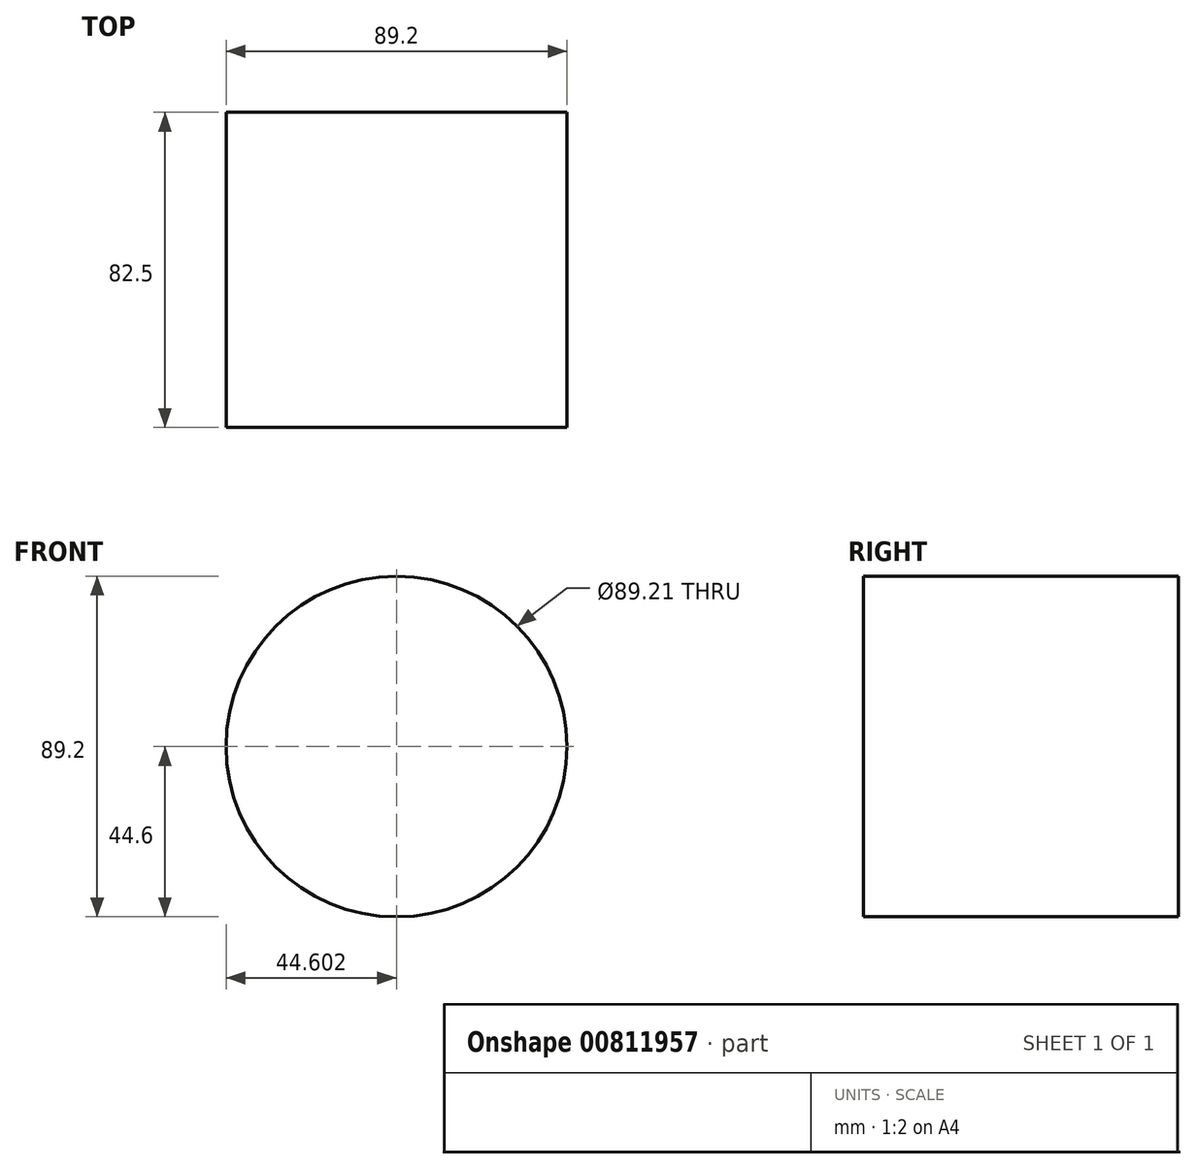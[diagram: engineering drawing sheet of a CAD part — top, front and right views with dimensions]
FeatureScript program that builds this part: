
annotation { "Feature Type Name" : "Feature", "Feature Type Description" : "" }
export const myFeature = defineFeature(function(context is Context, id is Id, definition is map)
    precondition{}
    {
        {
            var Q0;
            Q0=qCreatedBy(makeId("Top.planeOp"),FACE);
            var sketch = newSketch(context, id + "F0", { "sketchPlane" : qUnion([Q0])});
            skLineSegment(sketch, "E0.bottom", {"start": v(22.3, -41.25) * mm, "end": v(-22.3, -41.25) * mm});
            skLineSegment(sketch, "E0.top", {"start": v(22.3, 41.25) * mm, "end": v(-22.3, 41.25) * mm});
            skLineSegment(sketch, "E0.left", {"start": v(22.3, -41.25) * mm, "end": v(22.3, 41.25) * mm});
            skLineSegment(sketch, "E0.right", {"start": v(-22.3, -41.25) * mm, "end": v(-22.3, 41.25) * mm});
            skPoint(sketch, "E0.middle", {"position": v(0, 0) * mm});
            skLineSegment(sketch, "E1", {"start": v(-22.3, -41.25) * mm, "end": v(22.3, 41.25) * mm});
            skSolve(sketch);
        }
        {
            var Q0;
            Q0=makeQuery(id+"F0.imprint","IMPRINT",FACE,{"disambiguationData":[TD([[makeQuery(id+"F0.imprint","IMPRINT",EDGE,{"derivedFrom":sQuery(id+"F0.wireOp",EDGE,"E0.top")}),1.0]])]});
            var Q1;
            Q1=makeQuery(id+"F0.imprint","IMPRINT",FACE,{"disambiguationData":[TD([[makeQuery(id+"F0.imprint","IMPRINT",EDGE,{"derivedFrom":sQuery(id+"F0.wireOp",EDGE,"E0.bottom")}),-1.0]])]});
            var Q2;
            Q2=sQuery(id+"F0.wireOp",EDGE,"E0.right");
            var Q3;
            Q3=sQuery(id+"F0.wireOp",EDGE,"E0.left");
            revolve(context, id + "F1", {"bodyType" : ToolBodyType.SURFACE, "surfaceOperationType" : NewSurfaceOperationType.NEW, "entities" : qUnion([Q0, Q1]), "surfaceEntities" : qUnion([Q2]), "axis" : qUnion([Q3]), "revolveType" : RevolveType.FULL});
        }
    });
